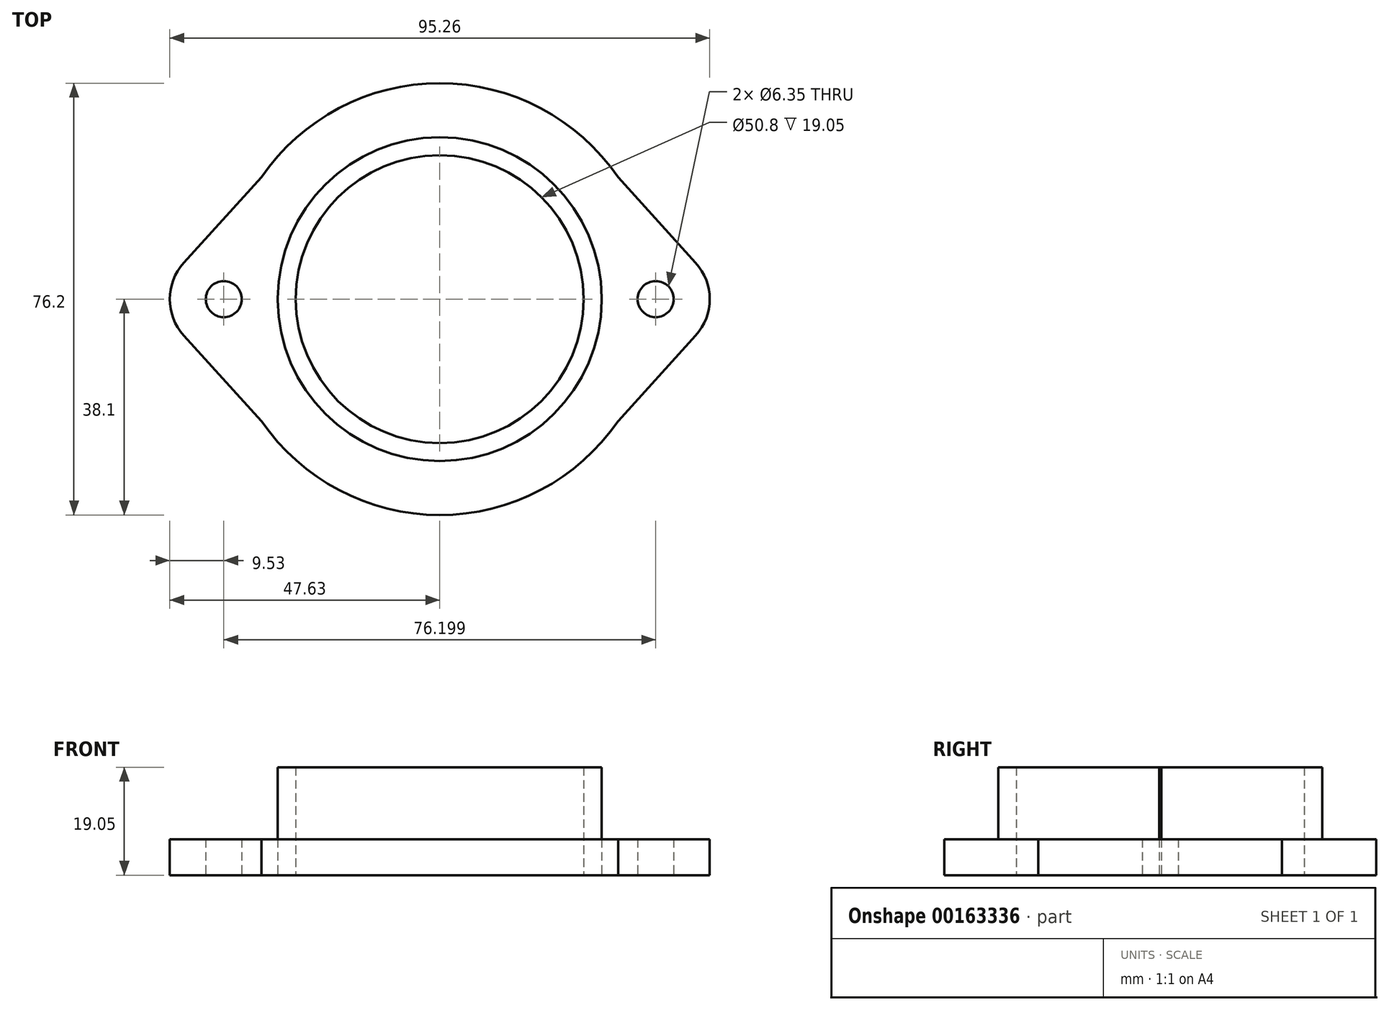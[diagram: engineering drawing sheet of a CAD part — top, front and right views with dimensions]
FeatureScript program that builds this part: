
annotation { "Feature Type Name" : "Feature", "Feature Type Description" : "" }
export const myFeature = defineFeature(function(context is Context, id is Id, definition is map)
    precondition{}
    {
        {
            var Q0;
            Q0=qCreatedBy(makeId("Top.planeOp"),FACE);
            var sketch = newSketch(context, id + "F0", { "sketchPlane" : qUnion([Q0])});
            skCircle(sketch, "E0", {"center": v(0, 0) * mm, "radius": 25.4 * mm});
            skCircle(sketch, "E1", {"center": v(0, 0) * mm, "radius": 28.58 * mm});
            skCircle(sketch, "E2", {"center": v(-38.1, 0) * mm, "radius": 3.18 * mm});
            skCircle(sketch, "E3", {"center": v(38.1, 0) * mm, "radius": 3.18 * mm});
            skArc(sketch, "E4", {"start": v(-45.16, 6.4) * mm, "mid": v(-47.63, 0) * mm, "end": v(-45.16, -6.4) * mm});
            skArc(sketch, "E5", {"start": v(28.57, 0.18) * mm, "mid": v(28.57, 0) * mm, "end": v(28.57, -0.18) * mm});
            skLineSegment(sketch, "E6", {"start": v(-45.16, 6.4) * mm, "end": v(-31.45, 21.5) * mm});
            skLineSegment(sketch, "E7", {"start": v(31.45, 21.5) * mm, "end": v(45.16, 6.4) * mm});
            skLineSegment(sketch, "E8", {"start": v(-31.45, -21.5) * mm, "end": v(-45.16, -6.4) * mm});
            skLineSegment(sketch, "E9", {"start": v(45.16, -6.4) * mm, "end": v(31.45, -21.5) * mm});
            skArc(sketch, "E10.trimOffspring", {"start": v(-28.57, -0.18) * mm, "mid": v(-28.57, 0) * mm, "end": v(-28.57, 0.18) * mm});
            skArc(sketch, "E11.trimOffspring", {"start": v(-31.45, -21.5) * mm, "mid": v(0, -38.1) * mm, "end": v(31.45, -21.5) * mm});
            skArc(sketch, "E12.trimOffspring", {"start": v(31.45, 21.5) * mm, "mid": v(0, 38.1) * mm, "end": v(-31.45, 21.5) * mm});
            skArc(sketch, "E13.trimOffspring", {"start": v(45.16, -6.4) * mm, "mid": v(47.63, 0) * mm, "end": v(45.16, 6.4) * mm});
            skSolve(sketch);
        }
        {
            var Q0;
            Q0=makeQuery(id+"F0.imprint","IMPRINT",FACE,{"disambiguationData":[TD([[makeQuery(id+"F0.imprint","IMPRINT",EDGE,{"derivedFrom":sQuery(id+"F0.wireOp",EDGE,"E0")}),-1.0]])]});
            extrude(context, id + "F1", {"entities" : qUnion([Q0]), "depth" : 19.05 * mm});
        }
        {
            var Q0;
            Q0 = qSketchRegion(id + "F0", true);
            extrude(context, id + "F2", {"entities" : qUnion([Q0]), "operationType" : NewBodyOperationType.ADD, "depth" : 6.35 * mm});
        }
    });
